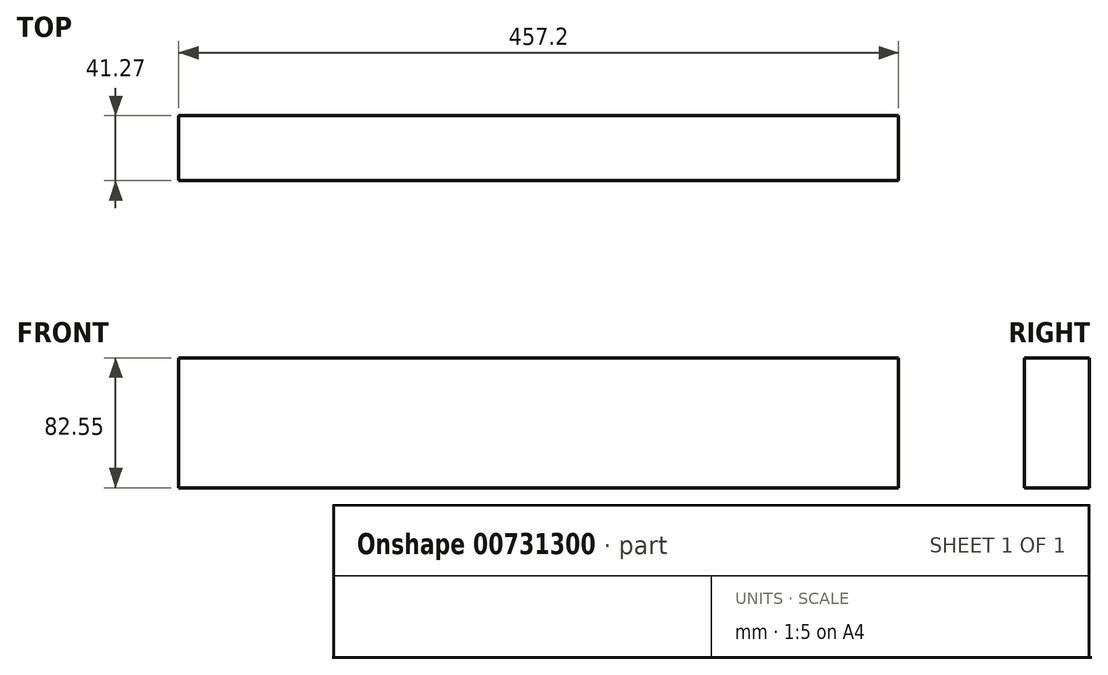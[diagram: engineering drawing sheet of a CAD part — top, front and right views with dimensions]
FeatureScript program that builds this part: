
annotation { "Feature Type Name" : "Feature", "Feature Type Description" : "" }
export const myFeature = defineFeature(function(context is Context, id is Id, definition is map)
    precondition{}
    {
        {
            var Q0;
            Q0=qCreatedBy(makeId("Front.planeOp"),FACE);
            var sketch = newSketch(context, id + "F0", { "sketchPlane" : qUnion([Q0])});
            skLineSegment(sketch, "E0.bottom", {"start": v(0, 0) * mm, "end": v(457.2, 0) * mm});
            skLineSegment(sketch, "E0.top", {"start": v(0, 82.55) * mm, "end": v(457.2, 82.55) * mm});
            skLineSegment(sketch, "E0.left", {"start": v(0, 0) * mm, "end": v(0, 82.55) * mm});
            skLineSegment(sketch, "E0.right", {"start": v(457.2, 0) * mm, "end": v(457.2, 82.55) * mm});
            skSolve(sketch);
        }
        {
            var Q0;
            Q0=makeQuery(id+"F0.imprint","IMPRINT",FACE,{"disambiguationData":[TD([[makeQuery(id+"F0.imprint","IMPRINT",EDGE,{"derivedFrom":sQuery(id+"F0.wireOp",EDGE,"E0.bottom")}),1.0]])]});
            extrude(context, id + "F1", {"entities" : qUnion([Q0]), "depth" : 41.27 * mm, "offsetDistance" : 25.4 * mm});
        }
    });
